# Revit family: 11436 Велопарковка «Бумеранг» Хоббика
name_source: partatom
category: Антураж
revit_build: Autodesk Revit 2018 (Build: 20180423_1000(x64)
units: mm (PartAtom-declared; Revit-internal decimal feet)

## family parameters
Всегда вертикально = Да
Источник визуального образа = Геометрия семейства
На основе рабочей плоскости = Нет
Общий = Нет
При загрузке вырезать с полостями = Нет
Точка расчета площади = Нет

## types (4) — shared parameters
URL = https://hobbyka.ru
Артикул товара = Арт. 11436
Высота = 1000 мм
Группа модели = Велопарковки
Изготовитель = ООО «Хоббика»
Изображение типоразмера = Велопарковка «Бумеранг» Арт 11436.jpeg
Ширина = 755 мм

## per-type parameters (varying)
| type | 6 мест | 9 мест | Версия 6 мест нержавеющая сталь | Версия 6 мест сталь | Версия 9 мест нержавеющая сталь | Версия 9 мест сталь | Длина | Материал изделия | Описание | Цвет каркаса |
| Версия 6 мест сталь | Да | Нет | Нет | Да | Нет | Нет | 1400 мм | Сталь | Велопарковка «Бумеранг». Версия 6 мест сталь | Сталь |
| Версия 6 мест нержавеющая сталь | Да | Нет | Да | Нет | Нет | Нет | 1400 мм | Нержавеющая сталь | Велопарковка «Бумеранг». Версия 6 мест нержавеющая сталь | Нержавеющая сталь |
| Версия 9 мест сталь | Нет | Да | Нет | Нет | Нет | Да | 2060 мм | Сталь | Велопарковка «Бумеранг». Версия 9 мест сталь | Сталь |
| Версия 9 мест нержавеющая сталь | Нет | Да | Нет | Нет | Да | Нет | 2060 мм | Нержавеющая сталь | Велопарковка «Бумеранг». Версия 9 мест нержавеющая сталь | Нержавеющая сталь |
